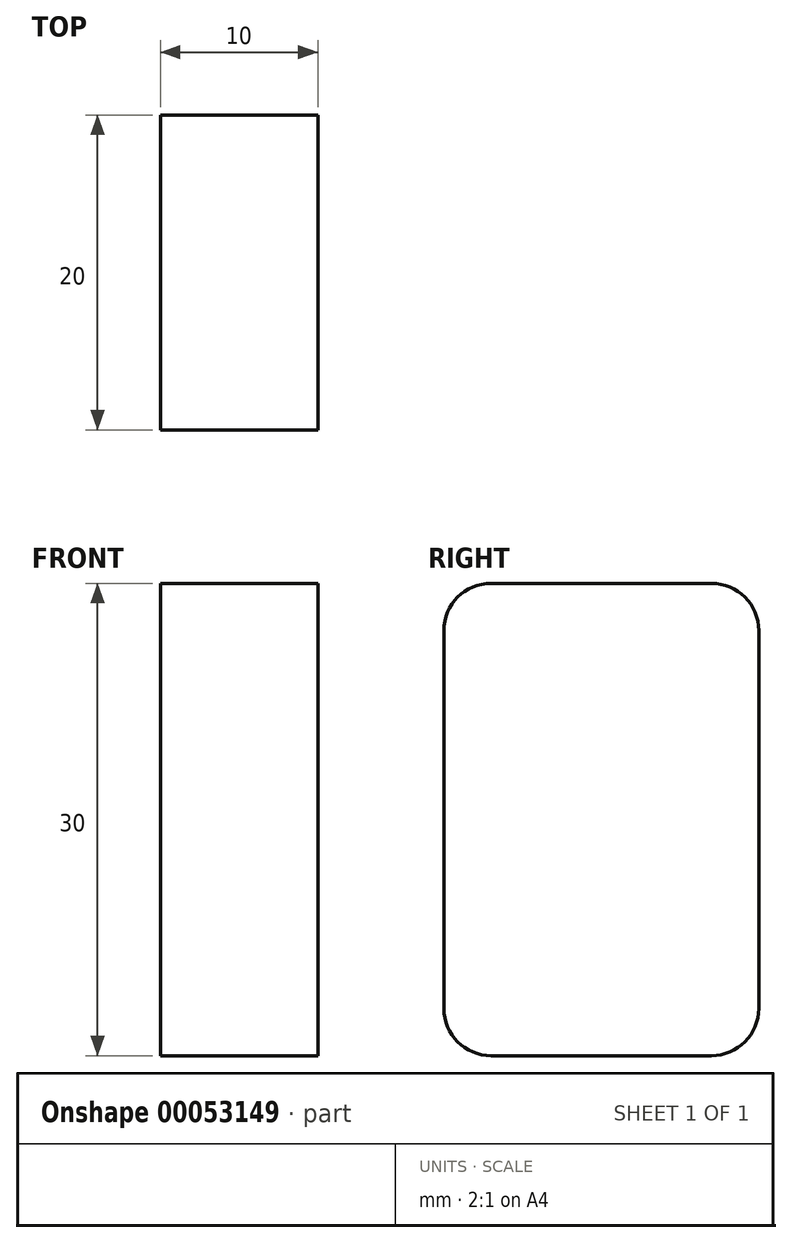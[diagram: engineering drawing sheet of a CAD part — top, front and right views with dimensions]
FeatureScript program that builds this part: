
annotation { "Feature Type Name" : "Feature", "Feature Type Description" : "" }
export const myFeature = defineFeature(function(context is Context, id is Id, definition is map)
    precondition{}
    {
        {
            var Q0;
            Q0=qCreatedBy(makeId("Top.planeOp"),FACE);
            var sketch = newSketch(context, id + "F0", { "sketchPlane" : qUnion([Q0])});
            skLineSegment(sketch, "E0.bottom", {"start": v(-69.48, 35.01) * mm, "end": v(-59.48, 35.01) * mm});
            skLineSegment(sketch, "E0.top", {"start": v(-69.48, 55.01) * mm, "end": v(-59.48, 55.01) * mm});
            skLineSegment(sketch, "E0.left", {"start": v(-69.48, 35.01) * mm, "end": v(-69.48, 55.01) * mm});
            skLineSegment(sketch, "E0.right", {"start": v(-59.48, 35.01) * mm, "end": v(-59.48, 55.01) * mm});
            skSolve(sketch);
        }
        {
            var Q0;
            Q0=makeQuery(id+"F0.imprint","IMPRINT",FACE,{"disambiguationData":[TD([[makeQuery(id+"F0.imprint","IMPRINT",EDGE,{"derivedFrom":sQuery(id+"F0.wireOp",EDGE,"E0.bottom")}),1.0]])]});
            extrude(context, id + "F1", {"entities" : qUnion([Q0]), "depth" : 30 * mm});
        }
        {
            var Q0;
            Q0=makeQuery(id+"F1.opExtrude","CAP_EDGE",EDGE,{"disambiguationData":[OSD([sQuery(id+"F0.wireOp",EDGE,"E0.top")])],"isStart":false});
            var Q1;
            Q1=makeQuery(id+"F1.opExtrude","CAP_EDGE",EDGE,{"disambiguationData":[OSD([sQuery(id+"F0.wireOp",EDGE,"E0.bottom")])],"isStart":false});
            var Q2;
            Q2=makeQuery(id+"F1.opExtrude","CAP_EDGE",EDGE,{"disambiguationData":[OSD([sQuery(id+"F0.wireOp",EDGE,"E0.top")])],"isStart":true});
            var Q3;
            Q3=makeQuery(id+"F1.opExtrude","CAP_EDGE",EDGE,{"disambiguationData":[OSD([sQuery(id+"F0.wireOp",EDGE,"E0.bottom")])],"isStart":true});
            fillet(context, id + "F2", {"entities" : qUnion([Q0, Q1, Q2, Q3]), "radius" : 3 * mm, "tangentPropagation" : true, "allowEdgeOverflow" : false});
        }
    });
